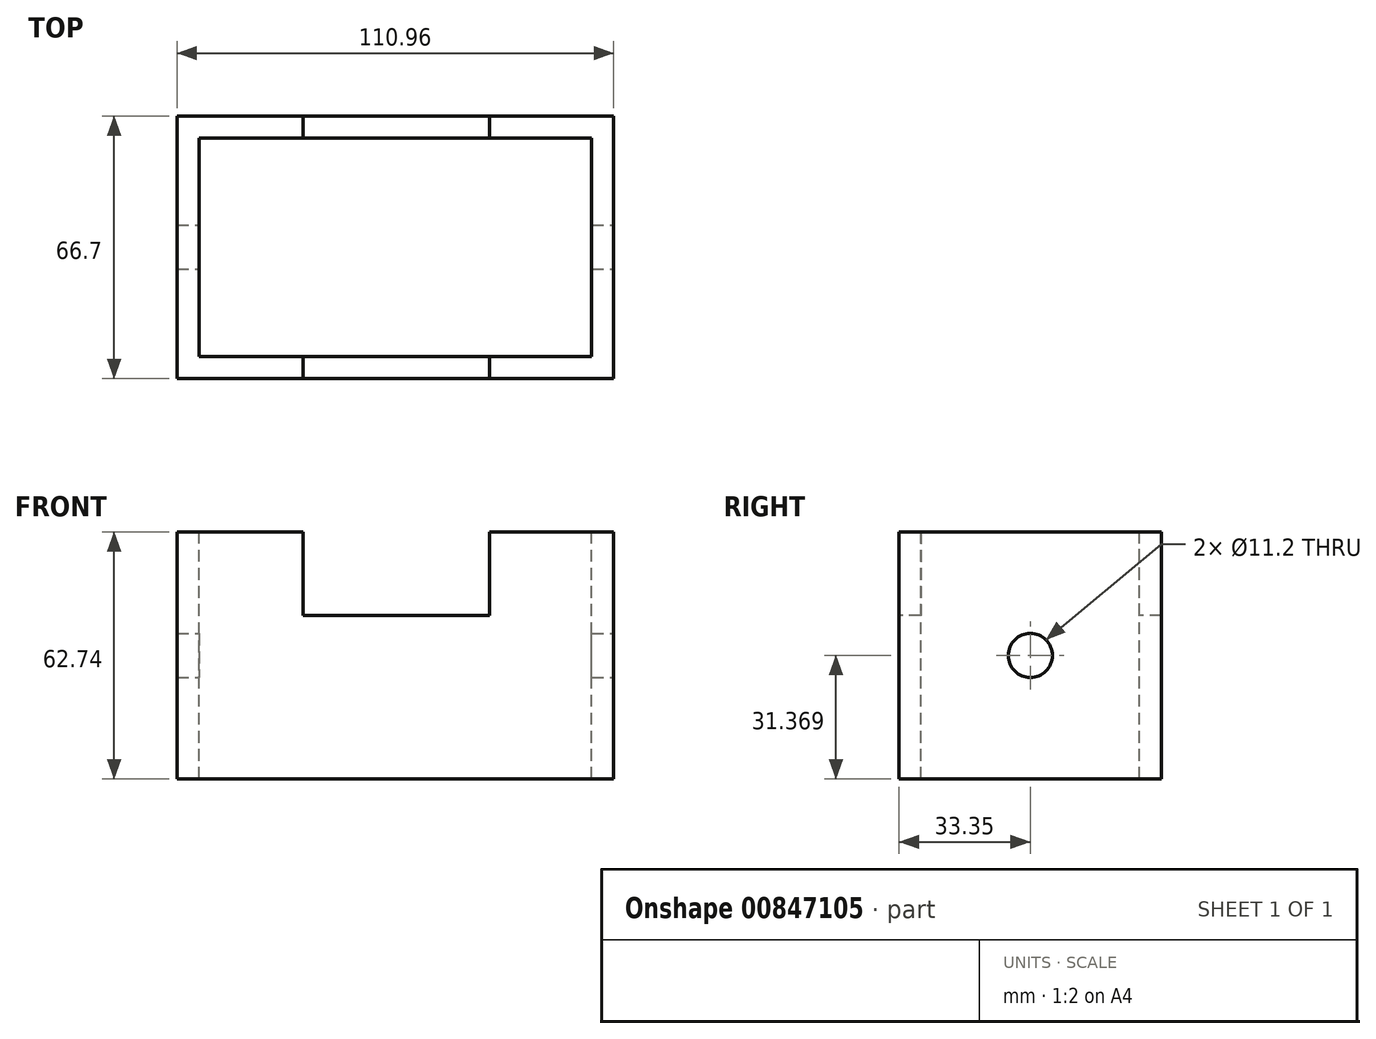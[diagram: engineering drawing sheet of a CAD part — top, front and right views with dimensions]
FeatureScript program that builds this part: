
annotation { "Feature Type Name" : "Feature", "Feature Type Description" : "" }
export const myFeature = defineFeature(function(context is Context, id is Id, definition is map)
    precondition{}
    {
        {
            var Q0;
            Q0=qCreatedBy(makeId("Top.planeOp"),FACE);
            var sketch = newSketch(context, id + "F0", { "sketchPlane" : qUnion([Q0])});
            skLineSegment(sketch, "E0.bottom", {"start": v(55.48, -33.35) * mm, "end": v(-55.48, -33.35) * mm});
            skLineSegment(sketch, "E0.top", {"start": v(55.48, 33.35) * mm, "end": v(-55.48, 33.35) * mm});
            skLineSegment(sketch, "E0.left", {"start": v(55.48, -33.35) * mm, "end": v(55.48, 33.35) * mm});
            skLineSegment(sketch, "E0.right", {"start": v(-55.48, -33.35) * mm, "end": v(-55.48, 33.35) * mm});
            skPoint(sketch, "E0.middle", {"position": v(0, 0) * mm});
            skSolve(sketch);
        }
        {
            var Q0;
            Q0 = qSketchRegion(id + "F0", true);
            extrude(context, id + "F1", {"entities" : qUnion([Q0]), "depth" : 62.74 * mm, "offsetDistance" : 25.4 * mm});
        }
        {
            var Q0;
            Q0=makeQuery(id+"F1.opExtrude","SWEPT_FACE",FACE,{"disambiguationData":[OSD([sQuery(id+"F0.wireOp",EDGE,"E0.left")])]});
            var sketch = newSketch(context, id + "F2", { "sketchPlane" : qUnion([Q0])});
            skLineSegment(sketch, "E1", {"start": v(0, 62.74) * mm, "end": v(0, 0) * mm, "construction": true});
            skCircle(sketch, "E2", {"center": v(0, 31.37) * mm, "radius": 5.6 * mm});
            skSolve(sketch);
        }
        {
            var Q0;
            Q0=makeQuery(id+"F2.imprint","IMPRINT",FACE,{"disambiguationData":[TD([[makeQuery(id+"F2.imprint","IMPRINT",EDGE,{"derivedFrom":sQuery(id+"F2.wireOp",EDGE,"E2")}),1.0]])]});
            extrude(context, id + "F3", {"entities" : qUnion([Q0]), "operationType" : NewBodyOperationType.REMOVE, "endBound" : BoundingType.THROUGH_ALL, "oppositeDirection" : true, "depth" : 25.4 * mm, "offsetDistance" : 25.4 * mm});
        }
        {
            var Q0;
            Q0=makeQuery(id+"F1.opExtrude","CAP_FACE",FACE,{"disambiguationData":[OSD([sQuery(id+"F0.wireOp",EDGE,"E0.bottom"),sQuery(id+"F0.wireOp",EDGE,"E0.top"),sQuery(id+"F0.wireOp",EDGE,"E0.left"),sQuery(id+"F0.wireOp",EDGE,"E0.right")])],"isStart":false});
            var sketch = newSketch(context, id + "F4", { "sketchPlane" : qUnion([Q0])});
            skLineSegment(sketch, "E3.0", {"start": v(49.89, -27.76) * mm, "end": v(49.89, 27.76) * mm});
            skLineSegment(sketch, "E3.1", {"start": v(-49.89, -27.76) * mm, "end": v(49.89, -27.76) * mm});
            skLineSegment(sketch, "E3.2", {"start": v(-49.89, 27.76) * mm, "end": v(-49.89, -27.76) * mm});
            skLineSegment(sketch, "E3.3", {"start": v(49.89, 27.76) * mm, "end": v(-49.89, 27.76) * mm});
            skSolve(sketch);
        }
        {
            var Q0;
            Q0=makeQuery(id+"F4.imprint","IMPRINT",FACE,{"disambiguationData":[TD([[makeQuery(id+"F4.imprint","IMPRINT",EDGE,{"derivedFrom":sQuery(id+"F4.wireOp",EDGE,"E3.0")}),1.0]])]});
            extrude(context, id + "F5", {"entities" : qUnion([Q0]), "operationType" : NewBodyOperationType.REMOVE, "endBound" : BoundingType.THROUGH_ALL, "oppositeDirection" : true, "depth" : 25.4 * mm, "offsetDistance" : 25.4 * mm});
        }
        {
            var Q0;
            Q0=makeQuery(id+"F1.opExtrude","SWEPT_FACE",FACE,{"disambiguationData":[OSD([sQuery(id+"F0.wireOp",EDGE,"E0.bottom")])]});
            var sketch = newSketch(context, id + "F6", { "sketchPlane" : qUnion([Q0])});
            skLineSegment(sketch, "E4", {"start": v(0, 0) * mm, "end": v(0, 62.74) * mm, "construction": true});
            skLineSegment(sketch, "E5.bottom", {"start": v(-23.48, 62.74) * mm, "end": v(23.93, 62.74) * mm});
            skLineSegment(sketch, "E5.top", {"start": v(-23.48, 41.59) * mm, "end": v(23.93, 41.59) * mm});
            skLineSegment(sketch, "E5.left", {"start": v(-23.48, 62.74) * mm, "end": v(-23.48, 41.59) * mm});
            skLineSegment(sketch, "E5.right", {"start": v(23.93, 62.74) * mm, "end": v(23.93, 41.59) * mm});
            skSolve(sketch);
        }
        {
            var Q0;
            Q0=makeQuery(id+"F6.imprint","IMPRINT",FACE,{"disambiguationData":[TD([[makeQuery(id+"F6.imprint","IMPRINT",EDGE,{"derivedFrom":sQuery(id+"F6.wireOp",EDGE,"E5.bottom")}),1.0]])]});
            extrude(context, id + "F7", {"entities" : qUnion([Q0]), "operationType" : NewBodyOperationType.REMOVE, "endBound" : BoundingType.THROUGH_ALL, "oppositeDirection" : true, "depth" : 25.4 * mm, "offsetDistance" : 25.4 * mm});
        }
    });
